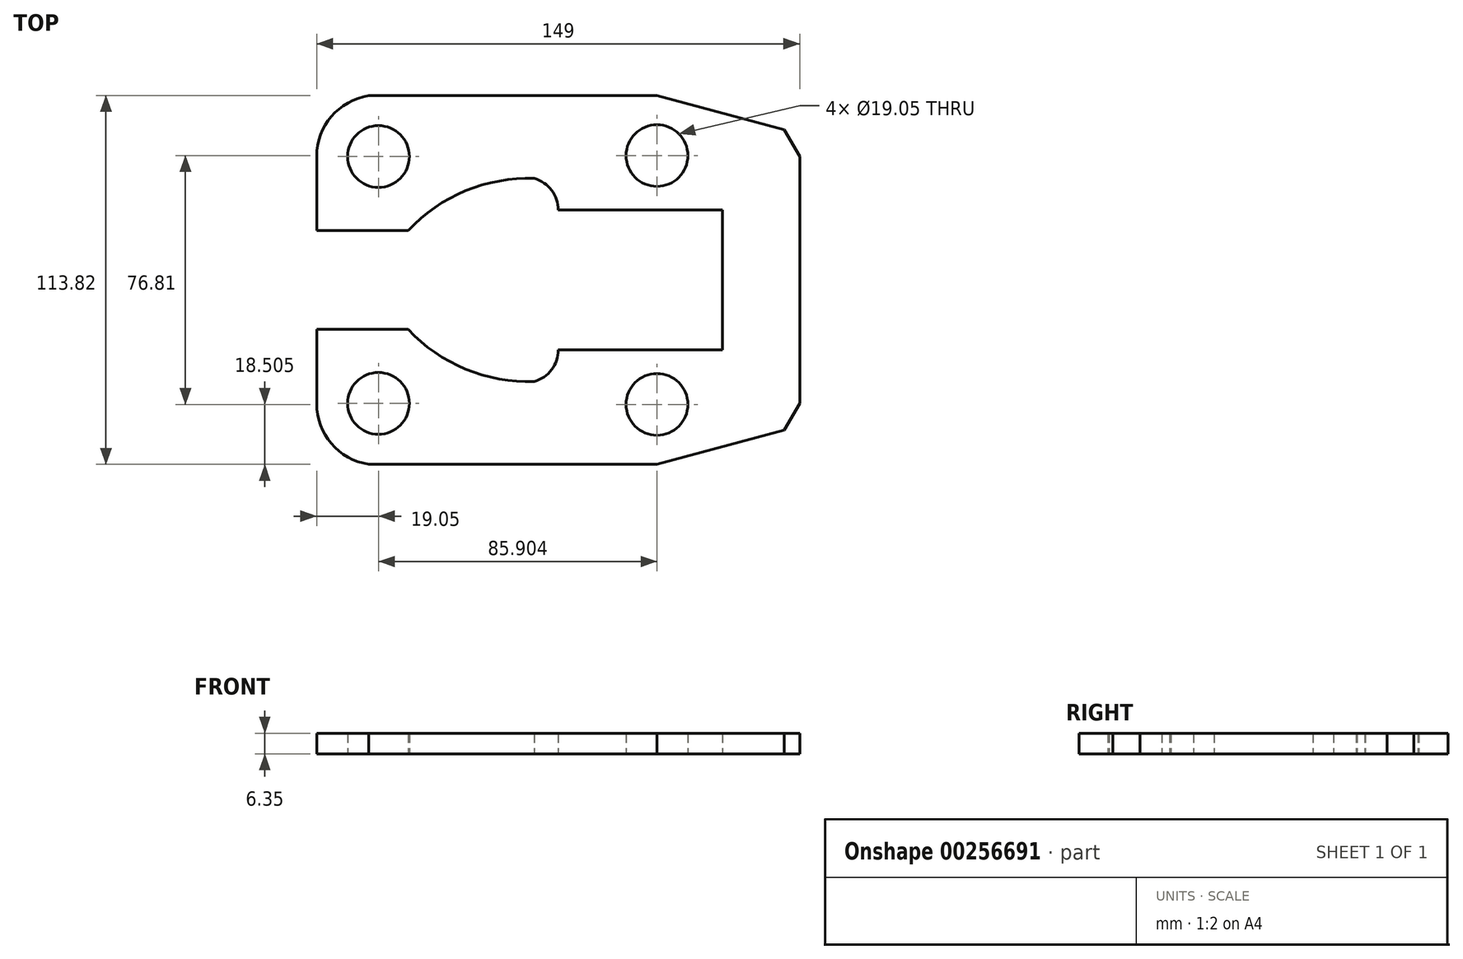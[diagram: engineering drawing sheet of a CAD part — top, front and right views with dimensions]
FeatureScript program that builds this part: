
annotation { "Feature Type Name" : "Feature", "Feature Type Description" : "" }
export const myFeature = defineFeature(function(context is Context, id is Id, definition is map)
    precondition{}
    {
        {
            var Q0;
            Q0=qCreatedBy(makeId("Top.planeOp"),FACE);
            var sketch = newSketch(context, id + "F0", { "sketchPlane" : qUnion([Q0])});
            skCircle(sketch, "E0", {"center": v(19.05, 38.1) * mm, "radius": 9.53 * mm});
            skArc(sketch, "E1", {"start": v(16.05, 56.91) * mm, "mid": v(4.56, 50.47) * mm, "end": v(0, 38.1) * mm});
            skLineSegment(sketch, "E2", {"start": v(0, 15.24) * mm, "end": v(28.19, 15.24) * mm});
            skLineSegment(sketch, "E3", {"start": v(16.05, 56.91) * mm, "end": v(104.95, 56.91) * mm});
            skLineSegment(sketch, "E4", {"start": v(0, 38.1) * mm, "end": v(0, 15.24) * mm});
            skCircle(sketch, "E5", {"center": v(104.95, 38.4) * mm, "radius": 9.53 * mm});
            skLineSegment(sketch, "E6", {"start": v(104.95, 56.91) * mm, "end": v(144.2, 46.4) * mm});
            skLineSegment(sketch, "E7", {"start": v(144.2, 46.4) * mm, "end": v(149, 38.1) * mm});
            skLineSegment(sketch, "E8", {"start": v(149, 38.1) * mm, "end": v(149, 0) * mm});
            skLineSegment(sketch, "E9", {"start": v(125.12, 21.57) * mm, "end": v(74.49, 21.57) * mm});
            skArc(sketch, "E10", {"start": v(74.49, 21.57) * mm, "mid": v(70.25, 29.82) * mm, "end": v(61.07, 31.19) * mm});
            skLineSegment(sketch, "E11.MirrorCS", {"start": v(0, -38.1) * mm, "end": v(0, -15.24) * mm});
            skLineSegment(sketch, "E12.MirrorCS", {"start": v(0, -15.24) * mm, "end": v(28.19, -15.24) * mm});
            skLineSegment(sketch, "E13.MirrorCS", {"start": v(125.12, -21.57) * mm, "end": v(74.49, -21.57) * mm});
            skLineSegment(sketch, "E14.MirrorCS", {"start": v(149, -38.1) * mm, "end": v(149, 0) * mm});
            skLineSegment(sketch, "E15.MirrorCS", {"start": v(144.2, -46.4) * mm, "end": v(149, -38.1) * mm});
            skLineSegment(sketch, "E16.MirrorCS", {"start": v(104.95, -56.91) * mm, "end": v(144.2, -46.4) * mm});
            skLineSegment(sketch, "E17.MirrorCS", {"start": v(16.05, -56.91) * mm, "end": v(104.95, -56.91) * mm});
            skArc(sketch, "E18.MirrorCS", {"start": v(16.05, -56.91) * mm, "mid": v(4.56, -50.47) * mm, "end": v(0, -38.1) * mm});
            skArc(sketch, "E19.MirrorC", {"start": v(74.49, -21.57) * mm, "mid": v(70.25, -29.82) * mm, "end": v(61.07, -31.19) * mm});
            skCircle(sketch, "E20.MirrorC", {"center": v(19.05, -38.1) * mm, "radius": 9.53 * mm});
            skCircle(sketch, "E21.MirrorC", {"center": v(104.95, -38.4) * mm, "radius": 9.53 * mm});
            skPoint(sketch, "E22.orphan", {"position": v(149, 21.57) * mm});
            skPoint(sketch, "E23.MirrorCS.end.orphan", {"position": v(125.12, -1.25) * mm});
            skPoint(sketch, "E23.MirrorCS.start.orphan", {"position": v(149, 0) * mm});
            skPoint(sketch, "E24.orphan", {"position": v(149, -21.57) * mm});
            skArc(sketch, "E25", {"start": v(67.13, 31.33) * mm, "mid": v(45.91, 27.51) * mm, "end": v(28.19, 15.24) * mm});
            skArc(sketch, "E26.MirrorCS", {"start": v(67.13, -31.33) * mm, "mid": v(45.91, -27.51) * mm, "end": v(28.19, -15.24) * mm});
            skPoint(sketch, "E27.orphan", {"position": v(56.38, 15.24) * mm});
            skPoint(sketch, "E28.orphan", {"position": v(56.38, -15.24) * mm});
            skPoint(sketch, "E29.orphan", {"position": v(0, 0) * mm});
            skPoint(sketch, "E30.start.orphan", {"position": v(125.12, 1.25) * mm});
            skLineSegment(sketch, "E31", {"start": v(125.12, -21.57) * mm, "end": v(125.12, 21.57) * mm});
            skSolve(sketch);
        }
        {
            var Q0;
            Q0=qSketchRegion(id+"F0",true);
            extrude(context, id + "F1", {"entities" : qUnion([Q0]), "depth" : 6.35 * mm});
        }
    });
